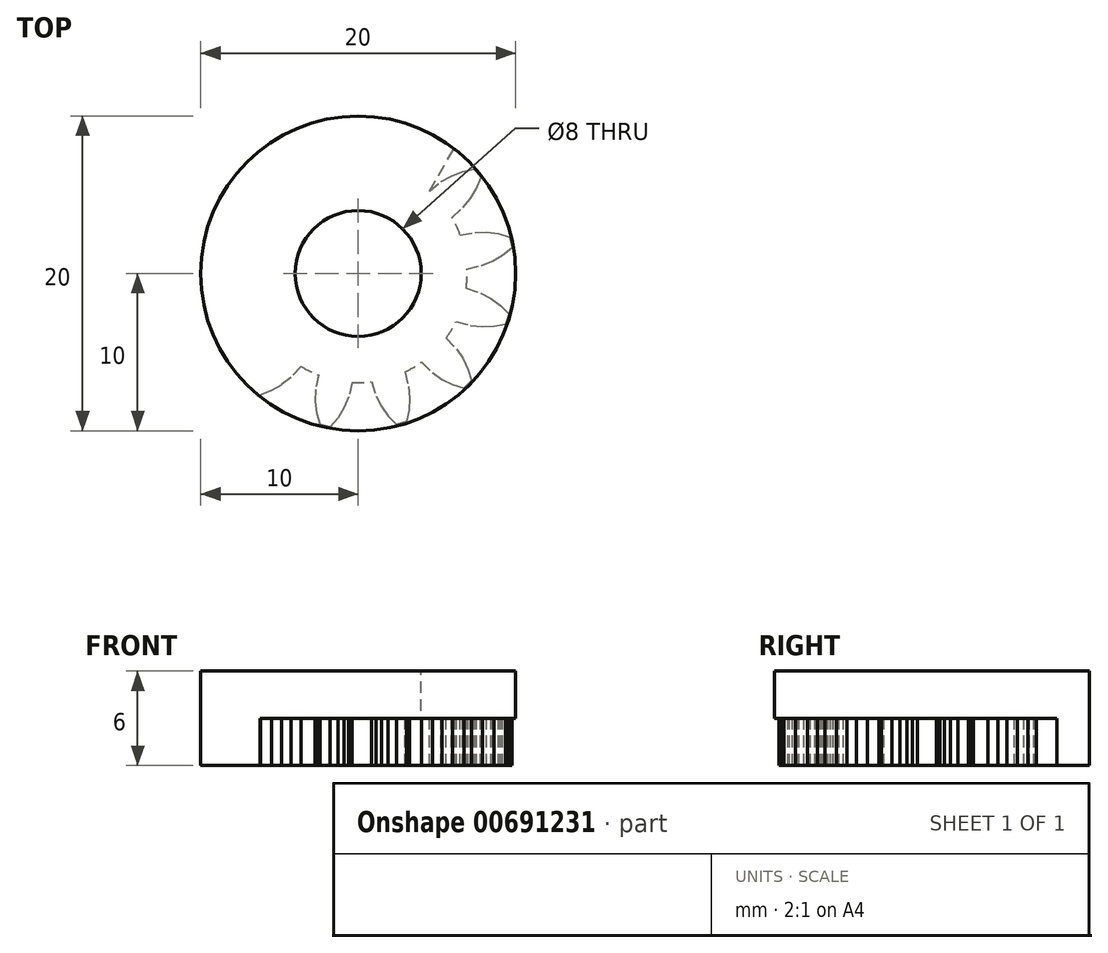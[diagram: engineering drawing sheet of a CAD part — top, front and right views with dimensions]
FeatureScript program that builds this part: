
annotation { "Feature Type Name" : "Feature", "Feature Type Description" : "" }
export const myFeature = defineFeature(function(context is Context, id is Id, definition is map)
    precondition{}
    {
        {
            var Q0;
            Q0=qCreatedBy(makeId("Top.planeOp"),FACE);
            var sketch = newSketch(context, id + "F0", { "sketchPlane" : qUnion([Q0])});
            skCircle(sketch, "E0", {"center": v(0, -55) * mm, "radius": 4 * mm});
            skCircle(sketch, "E1", {"center": v(0, -55) * mm, "radius": 10 * mm});
            skSolve(sketch);
        }
        {
            var Q0;
            Q0=makeQuery(id+"F0.imprint","IMPRINT",FACE,{"disambiguationData":[TD([[makeQuery(id+"F0.imprint","IMPRINT",EDGE,{"derivedFrom":sQuery(id+"F0.wireOp",EDGE,"UXTzx6qa-yhJH-ITIm-0ZTv-eja71HHoNNuS")}),-1.0]])]});
            var Q1;
            Q1=makeQuery(id+"F0.imprint","IMPRINT",FACE,{"disambiguationData":[TD([[makeQuery(id+"F0.imprint","IMPRINT",EDGE,{"derivedFrom":sQuery(id+"F0.wireOp",EDGE,"E0")}),-1.0]])]});
            var Q2;
            Q2=makeQuery(id+"F0.imprint","IMPRINT",FACE,{"disambiguationData":[TD([[makeQuery(id+"F0.imprint","IMPRINT",EDGE,{"derivedFrom":sQuery(id+"F0.wireOp",EDGE,"GlbpL8rc-nhBS-EUnI-tKOA-gJgQpF3go9I5")}),-1.0]])]});
            extrude(context, id + "F1", {"entities" : qUnion([Q0, Q1, Q2]), "oppositeDirection" : true, "depth" : 3 * mm, "offsetDistance" : 25 * mm});
        }
        {
            var Q0;
            Q0=makeQuery(id+"F1.opExtrude","CAP_FACE",FACE,{"disambiguationData":[OSD([sQuery(id+"F0.wireOp",EDGE,"UXTzx6qa-yhJH-ITIm-0ZTv-eja71HHoNNuS"),sQuery(id+"F0.wireOp",EDGE,"GlbpL8rc-nhBS-EUnI-tKOA-gJgQpF3go9I5"),sQuery(id+"F0.wireOp",EDGE,"CqDqJyvB-gGjX-meG5-vYmM-PxKgu8H326RP"),sQuery(id+"F0.wireOp",EDGE,"fvICRfom-d5Nr-3mFn-KT7T-rGq5uc7C9K1d"),sQuery(id+"F0.wireOp",EDGE,"vQQ88SEw-eiIb-VBOH-OGII-zZQVb1DxRWrS"),sQuery(id+"F0.wireOp",EDGE,"2SCETibW-Yxqs-4xL1-Gk6n-E0inLarlBe3j"),sQuery(id+"F0.wireOp",EDGE,"E0"),sQuery(id+"F0.wireOp",EDGE,"W5f8Jsbh-s0gC-Mpse-dFM0-Er1Iplnl4nS4"),sQuery(id+"F0.wireOp",EDGE,"w1YcW64Q-Da9R-EJqw-NC6I-KFqnrBhOD4dZ"),sQuery(id+"F0.wireOp",EDGE,"pFIso20s-onKK-gejC-7una-TZNaoAULAibU"),sQuery(id+"F0.wireOp",EDGE,"nekmmUvM-RxUy-I8sp-ACT9-S1TbsbI0WVxJ"),sQuery(id+"F0.wireOp",EDGE,"dd27f826-d2e8-4011-8547-29bb10dc94730.MirrorCS"),sQuery(id+"F0.wireOp",EDGE,"387ca3d8-4a95-4597-a9b0-377f1fa871430.MirrorCS"),sQuery(id+"F0.wireOp",EDGE,"6877f961-c541-469a-aa6b-c69f784bd6da0.MirrorCS")])],"isStart":true});
            var sketch = newSketch(context, id + "F2", { "sketchPlane" : qUnion([Q0])});
            skCircle(sketch, "E2", {"center": v(0, -55) * mm, "radius": 9.9 * mm, "construction": true});
            skCircle(sketch, "E3", {"center": v(0, -55) * mm, "radius": 6.93 * mm});
            skLineSegment(sketch, "E4", {"start": v(4.53, -49.76) * mm, "end": v(5.28, -49.17) * mm});
            skLineSegment(sketch, "E5", {"start": v(5.28, -49.17) * mm, "end": v(5.93, -48.8) * mm});
            skLineSegment(sketch, "E6", {"start": v(5.93, -48.8) * mm, "end": v(6.63, -48.54) * mm});
            skLineSegment(sketch, "E7", {"start": v(6.63, -48.54) * mm, "end": v(7.36, -48.38) * mm});
            skLineSegment(sketch, "E8", {"start": v(7.36, -48.38) * mm, "end": v(7.8, -48.9) * mm});
            skLineSegment(sketch, "E9", {"start": v(7.58, -48.64) * mm, "end": v(0, -55) * mm, "construction": true});
            skLineSegment(sketch, "E10", {"start": v(0, -55.7) * mm, "end": v(0, -55) * mm, "construction": true});
            skLineSegment(sketch, "E11.MirrorCS", {"start": v(7.8, -48.9) * mm, "end": v(7.36, -48.38) * mm});
            skLineSegment(sketch, "E12.MirrorCS", {"start": v(7.13, -50.24) * mm, "end": v(7.51, -49.6) * mm});
            skLineSegment(sketch, "E13.MirrorCS", {"start": v(6.65, -50.82) * mm, "end": v(7.13, -50.24) * mm});
            skLineSegment(sketch, "E14.MirrorCS", {"start": v(5.95, -51.45) * mm, "end": v(6.65, -50.82) * mm});
            skLineSegment(sketch, "E15.MirrorCS", {"start": v(7.51, -49.6) * mm, "end": v(7.8, -48.9) * mm});
            skLineSegment(sketch, "E16.1.0", {"start": v(6.92, -54.71) * mm, "end": v(7.84, -54.5) * mm});
            skLineSegment(sketch, "E16.1.1", {"start": v(7.84, -54.5) * mm, "end": v(8.54, -54.21) * mm});
            skLineSegment(sketch, "E16.1.2", {"start": v(8.54, -54.21) * mm, "end": v(9.18, -53.83) * mm});
            skLineSegment(sketch, "E16.1.3", {"start": v(9.18, -53.83) * mm, "end": v(9.76, -53.35) * mm});
            skLineSegment(sketch, "E16.1.4", {"start": v(6.48, -52.55) * mm, "end": v(7.41, -52.4) * mm});
            skLineSegment(sketch, "E16.1.5", {"start": v(7.41, -52.4) * mm, "end": v(8.16, -52.38) * mm});
            skLineSegment(sketch, "E16.1.6", {"start": v(8.16, -52.38) * mm, "end": v(8.9, -52.48) * mm});
            skLineSegment(sketch, "E16.1.7", {"start": v(8.9, -52.48) * mm, "end": v(9.63, -52.69) * mm});
            skLineSegment(sketch, "E16.1.8", {"start": v(9.63, -52.69) * mm, "end": v(9.76, -53.35) * mm});
            skLineSegment(sketch, "E16.1.9", {"start": v(9.76, -53.35) * mm, "end": v(9.63, -52.69) * mm});
            skLineSegment(sketch, "E16.2.0", {"start": v(6.22, -58.04) * mm, "end": v(7.14, -58.3) * mm});
            skLineSegment(sketch, "E16.2.1", {"start": v(7.14, -58.3) * mm, "end": v(7.88, -58.37) * mm});
            skLineSegment(sketch, "E16.2.2", {"start": v(7.88, -58.37) * mm, "end": v(8.63, -58.34) * mm});
            skLineSegment(sketch, "E16.2.3", {"start": v(8.63, -58.34) * mm, "end": v(9.37, -58.2) * mm});
            skLineSegment(sketch, "E16.2.4", {"start": v(6.86, -55.93) * mm, "end": v(7.76, -56.24) * mm});
            skLineSegment(sketch, "E16.2.5", {"start": v(7.76, -56.24) * mm, "end": v(8.43, -56.58) * mm});
            skLineSegment(sketch, "E16.2.6", {"start": v(8.43, -56.58) * mm, "end": v(9.03, -57.03) * mm});
            skLineSegment(sketch, "E16.2.7", {"start": v(9.03, -57.03) * mm, "end": v(9.56, -57.56) * mm});
            skLineSegment(sketch, "E16.2.8", {"start": v(9.56, -57.56) * mm, "end": v(9.37, -58.2) * mm});
            skLineSegment(sketch, "E16.2.9", {"start": v(9.37, -58.2) * mm, "end": v(9.56, -57.56) * mm});
            skLineSegment(sketch, "E16.anchor1", {"start": v(0, -55) * mm, "end": v(4.53, -49.76) * mm, "construction": true});
            skLineSegment(sketch, "E16.anchor2", {"start": v(0, -55) * mm, "end": v(-3.63, -60.9) * mm, "construction": true});
            skLineSegment(sketch, "E17.3.3.0", {"start": v(4.7, -61.3) * mm, "end": v(5.32, -61.72) * mm});
            skLineSegment(sketch, "E17.6.3.0", {"start": v(5.32, -61.72) * mm, "end": v(6, -62.05) * mm});
            skLineSegment(sketch, "E17.9.3.0", {"start": v(6, -62.05) * mm, "end": v(6.71, -62.28) * mm});
            skLineSegment(sketch, "E17.12.3.0", {"start": v(5.59, -59.1) * mm, "end": v(6.23, -59.79) * mm});
            skLineSegment(sketch, "E17.13.3.0", {"start": v(4.02, -60.64) * mm, "end": v(4.7, -61.3) * mm});
            skLineSegment(sketch, "E17.15.3.0", {"start": v(6.23, -59.79) * mm, "end": v(6.65, -60.4) * mm});
            skLineSegment(sketch, "E17.18.3.0", {"start": v(6.65, -60.4) * mm, "end": v(6.98, -61.09) * mm});
            skLineSegment(sketch, "E17.21.3.0", {"start": v(6.98, -61.09) * mm, "end": v(7.2, -61.8) * mm});
            skLineSegment(sketch, "E17.24.3.0", {"start": v(7.2, -61.8) * mm, "end": v(6.71, -62.28) * mm});
            skLineSegment(sketch, "E17.27.3.0", {"start": v(6.71, -62.28) * mm, "end": v(7.2, -61.8) * mm});
            skLineSegment(sketch, "E17.3.4.0", {"start": v(1.14, -62.78) * mm, "end": v(1.48, -63.45) * mm});
            skLineSegment(sketch, "E17.6.4.0", {"start": v(1.48, -63.45) * mm, "end": v(1.91, -64.06) * mm});
            skLineSegment(sketch, "E17.9.4.0", {"start": v(1.91, -64.06) * mm, "end": v(2.43, -64.6) * mm});
            skLineSegment(sketch, "E17.12.4.0", {"start": v(2.96, -61.26) * mm, "end": v(3.2, -62.18) * mm});
            skLineSegment(sketch, "E17.13.4.0", {"start": v(0.85, -61.87) * mm, "end": v(1.14, -62.78) * mm});
            skLineSegment(sketch, "E17.15.4.0", {"start": v(3.2, -62.18) * mm, "end": v(3.27, -62.92) * mm});
            skLineSegment(sketch, "E17.18.4.0", {"start": v(3.27, -62.92) * mm, "end": v(3.23, -63.67) * mm});
            skLineSegment(sketch, "E17.21.4.0", {"start": v(3.23, -63.67) * mm, "end": v(3.08, -64.4) * mm});
            skLineSegment(sketch, "E17.24.4.0", {"start": v(3.08, -64.4) * mm, "end": v(2.43, -64.6) * mm});
            skLineSegment(sketch, "E17.27.4.0", {"start": v(2.43, -64.6) * mm, "end": v(3.08, -64.4) * mm});
            skLineSegment(sketch, "E17.3.5.0", {"start": v(-2.7, -62.38) * mm, "end": v(-2.73, -63.13) * mm});
            skLineSegment(sketch, "E17.6.5.0", {"start": v(-2.73, -63.13) * mm, "end": v(-2.64, -63.87) * mm});
            skLineSegment(sketch, "E17.9.5.0", {"start": v(-2.64, -63.87) * mm, "end": v(-2.43, -64.6) * mm});
            skLineSegment(sketch, "E17.12.5.0", {"start": v(-0.38, -61.91) * mm, "end": v(-0.6, -62.84) * mm});
            skLineSegment(sketch, "E17.13.5.0", {"start": v(-2.53, -61.45) * mm, "end": v(-2.7, -62.38) * mm});
            skLineSegment(sketch, "E17.15.5.0", {"start": v(-0.6, -62.84) * mm, "end": v(-0.9, -63.53) * mm});
            skLineSegment(sketch, "E17.18.5.0", {"start": v(-0.9, -63.53) * mm, "end": v(-1.29, -64.17) * mm});
            skLineSegment(sketch, "E17.21.5.0", {"start": v(-1.29, -64.17) * mm, "end": v(-1.77, -64.74) * mm});
            skLineSegment(sketch, "E17.24.5.0", {"start": v(-1.77, -64.74) * mm, "end": v(-2.43, -64.6) * mm});
            skLineSegment(sketch, "E17.27.5.0", {"start": v(-2.43, -64.6) * mm, "end": v(-1.77, -64.74) * mm});
            skLineSegment(sketch, "E18.3.6.0", {"start": v(-5.9, -60.2) * mm, "end": v(-6.27, -60.85) * mm});
            skLineSegment(sketch, "E18.6.6.0", {"start": v(-6.27, -60.85) * mm, "end": v(-6.55, -61.55) * mm});
            skLineSegment(sketch, "E18.9.6.0", {"start": v(-6.55, -61.55) * mm, "end": v(-6.71, -62.28) * mm});
            skLineSegment(sketch, "E18.12.6.0", {"start": v(-3.63, -60.9) * mm, "end": v(-4.27, -61.6) * mm});
            skLineSegment(sketch, "E18.13.6.0", {"start": v(-5.3, -59.46) * mm, "end": v(-5.9, -60.2) * mm});
            skLineSegment(sketch, "E18.15.6.0", {"start": v(-4.27, -61.6) * mm, "end": v(-4.85, -62.07) * mm});
            skLineSegment(sketch, "E18.18.6.0", {"start": v(-4.85, -62.07) * mm, "end": v(-5.5, -62.44) * mm});
            skLineSegment(sketch, "E18.21.6.0", {"start": v(-5.5, -62.44) * mm, "end": v(-6.2, -62.72) * mm});
            skLineSegment(sketch, "E18.24.6.0", {"start": v(-6.2, -62.72) * mm, "end": v(-6.71, -62.28) * mm});
            skLineSegment(sketch, "E18.27.6.0", {"start": v(-6.71, -62.28) * mm, "end": v(-6.2, -62.72) * mm});
            skLineSegment(sketch, "E19", {"start": v(4.53, -49.76) * mm, "end": v(6.1, -47.07) * mm});
            skLineSegment(sketch, "E20", {"start": v(-5.3, -59.46) * mm, "end": v(-6.23, -62.82) * mm});
            skSolve(sketch);
        }
        {
            var Q0;
            Q0=makeQuery(id+"F2.imprint","IMPRINT",FACE,{"disambiguationData":[TD([[makeQuery(id+"F2.imprint","IMPRINT",EDGE,{"derivedFrom":sQuery(id+"F2.wireOp",EDGE,"E4")}),1.0]])]});
            extrude(context, id + "F3", {"entities" : qUnion([Q0]), "operationType" : NewBodyOperationType.REMOVE, "oppositeDirection" : true, "depth" : 25 * mm, "offsetDistance" : 25 * mm});
        }
        {
            var Q0;
            Q0=makeQuery(id+"F0.imprint","IMPRINT",FACE,{"disambiguationData":[TD([[makeQuery(id+"F0.imprint","IMPRINT",EDGE,{"derivedFrom":sQuery(id+"F0.wireOp",EDGE,"E0")}),-1.0]])]});
            extrude(context, id + "F4", {"entities" : qUnion([Q0]), "operationType" : NewBodyOperationType.ADD, "depth" : 3 * mm, "offsetDistance" : 25 * mm});
        }
    });
